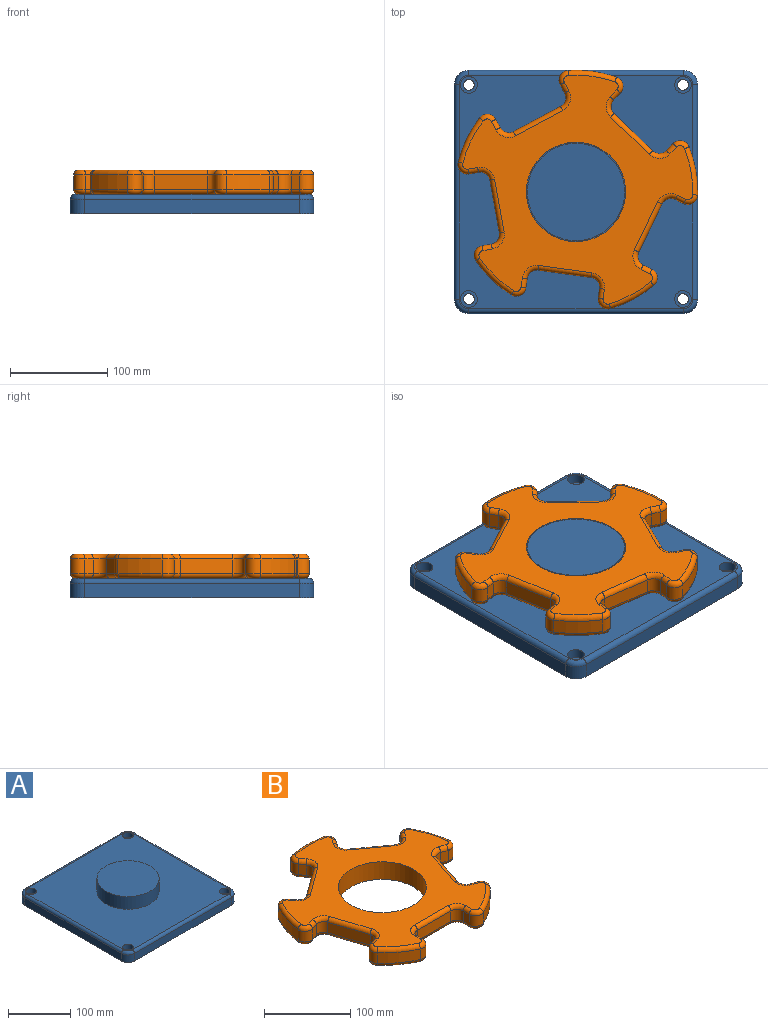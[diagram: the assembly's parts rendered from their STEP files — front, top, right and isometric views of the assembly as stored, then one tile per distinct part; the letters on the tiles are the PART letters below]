
ASSEMBLY  parts=2 mates=1
PART A: 32 faces, bbox 252.5x252.5x45 mm
  f0: plane 220x15mm, normal (1,0,0), area 3300mm2, adj f5,f8,f11,f27
  f1: plane 220x15mm, normal (0,1,0), area 3300mm2, adj f5,f8,f9,f31
  f2: plane 220x15mm, normal (-1,0,0), area 3300mm2, adj f5,f9,f10,f28
  f3: plane 220x15mm, normal (0,-1,0), area 3300mm2, adj f5,f10,f11,f24
  f4: plane 240x240mm, normal (0,0,1), area 48725.4mm2, adj f6,f14,f17,f20,f23,f24,f25,f26
  f5: plane 250x250mm, normal (0,0,-1), area 61926.7mm2, adj f0,f1,f2,f3,f8,f9,f10,f11
  f6: cylinder r=50mm len=100mm, axis (0,0,-1), area 7854mm2, adj f4,f7
  f7: plane 100x100mm, normal (0,0,1), area 7854mm2, adj f6
  f8: cylinder r=15mm len=15mm, axis (0,0,-1), area 353.4mm2, adj f0,f1,f5,f29
  f9: cylinder r=15mm len=15mm, axis (0,0,1), area 353.4mm2, adj f1,f2,f5,f30
  f10: cylinder r=15mm len=15mm, axis (0,0,-1), area 353.4mm2, adj f2,f3,f5,f26
  f11: cylinder r=15mm len=15mm, axis (0,0,1), area 353.4mm2, adj f0,f3,f5,f25
  f12: cylinder r=5.5mm len=11mm, axis (0,0,1), area 345.6mm2, adj f5,f13
  f13: plane 17.25x17.25mm, normal (0,0,1), area 138.7mm2, adj f12,f14
  f14: cylinder r=8.62mm len=17.25mm, axis (0,0,1), area 541.9mm2, adj f4,f13
  f15: cylinder r=5.5mm len=11mm, axis (0,0,1), area 345.6mm2, adj f5,f16
  f16: plane 17.25x17.25mm, normal (0,0,1), area 138.7mm2, adj f15,f17
  f17: cylinder r=8.62mm len=17.25mm, axis (0,0,1), area 541.9mm2, adj f4,f16
  f18: cylinder r=5.5mm len=11mm, axis (0,0,1), area 345.6mm2, adj f5,f19
  f19: plane 17.25x17.25mm, normal (0,0,1), area 138.7mm2, adj f18,f20
  f20: cylinder r=8.62mm len=17.25mm, axis (0,0,1), area 541.9mm2, adj f4,f19
  f21: cylinder r=5.5mm len=11mm, axis (0,0,1), area 345.6mm2, adj f5,f22
  f22: plane 17.25x17.25mm, normal (0,0,1), area 138.7mm2, adj f21,f23
  f23: cylinder r=8.62mm len=17.25mm, axis (0,0,1), area 541.9mm2, adj f4,f22
  f24: cylinder r=5mm len=220mm, axis (-1,0,0), area 1727.9mm2, adj f3,f4,f25,f26
  f25: torus R=10mm, axis (0,0,1), area 162.6mm2, adj f4,f11,f24,f27
  f26: torus R=10mm, axis (0,0,1), area 162.6mm2, adj f4,f10,f24,f28
  f27: cylinder r=5mm len=220mm, axis (0,-1,0), area 1727.9mm2, adj f0,f4,f25,f29
  f28: cylinder r=5mm len=220mm, axis (0,1,0), area 1727.9mm2, adj f2,f4,f26,f30
  f29: torus R=10mm, axis (0,0,1), area 162.6mm2, adj f4,f8,f27,f31
  f30: torus R=10mm, axis (0,0,1), area 162.6mm2, adj f4,f9,f28,f31
  f31: cylinder r=5mm len=220mm, axis (1,0,0), area 1727.9mm2, adj f1,f4,f29,f30
PART B: 123 faces, bbox 268.9x258.5x25 mm
  f0: plane 238.57x229.73mm, normal (0,0,1), area 21505.7mm2, adj f6,f43,f44,f45,f46,f47,f48,f49
  f1: plane 238.57x229.73mm, normal (0,0,-1), area 21505.7mm2, adj f6,f83,f84,f85,f86,f87,f88,f89
  f2: cylinder r=125mm len=40.68mm, axis (0,0,-1), area 759.5mm2, adj f13,f42,f51,f91
  f3: cylinder r=125mm len=47.82mm, axis (0,0,-1), area 759.5mm2, adj f35,f41,f67,f107
  f4: cylinder r=125mm len=50.29mm, axis (0,0,-1), area 759.5mm2, adj f28,f34,f82,f122
  f5: cylinder r=125mm len=47.82mm, axis (0,0,-1), area 759.5mm2, adj f21,f27,f66,f106
  f6: cylinder r=51mm len=102mm, axis (0,0,-1), area 8011.1mm2, adj f0,f1
  f7: cylinder r=125mm len=40.68mm, axis (0,0,-1), area 759.5mm2, adj f14,f20,f50,f90
  f8: plane 15x9.73mm, normal (-1,0,0), area 146mm2, adj f11,f14,f46,f86
  f9: plane 55x15mm, normal (0,-1,0), area 825mm2, adj f11,f12,f43,f83
  f10: plane 15x9.73mm, normal (1,0,0), area 146mm2, adj f12,f13,f47,f87
  f11: cylinder r=10mm len=15mm, axis (0,0,-1), area 235.6mm2, adj f8,f9,f44,f84
  f12: cylinder r=10mm len=15mm, axis (0,0,-1), area 235.6mm2, adj f9,f10,f45,f85
  f13: cylinder r=10mm len=15mm, axis (0,0,-1), area 299.5mm2, adj f2,f10,f49,f89
  f14: cylinder r=10mm len=15mm, axis (0,0,-1), area 299.5mm2, adj f7,f8,f48,f88
  f15: plane 15x9.26mm, normal (-0.31,-0.95,0), area 146mm2, adj f18,f21,f62,f102
  f16: plane 52.31x17mm, normal (0.95,-0.31,0), area 825mm2, adj f18,f19,f58,f98
  f17: plane 15x9.26mm, normal (0.31,0.95,0), area 146mm2, adj f19,f20,f54,f94
  f18: cylinder r=10mm len=15mm, axis (0,0,-1), area 235.6mm2, adj f15,f16,f60,f100
  f19: cylinder r=10mm len=15mm, axis (0,0,-1), area 235.6mm2, adj f16,f17,f56,f96
  f20: cylinder r=10mm len=16.25mm, axis (0,0,-1), area 299.5mm2, adj f7,f17,f52,f92
  f21: cylinder r=10mm len=15mm, axis (0,0,-1), area 299.5mm2, adj f5,f15,f64,f104
  f22: plane 15x7.87mm, normal (0.81,-0.59,0), area 146mm2, adj f25,f28,f78,f118
  f23: plane 44.5x32.33mm, normal (0.59,0.81,0), area 825mm2, adj f25,f26,f74,f114
  f24: plane 15x7.87mm, normal (-0.81,0.59,0), area 146mm2, adj f26,f27,f70,f110
  f25: cylinder r=10mm len=15mm, axis (0,0,-1), area 235.6mm2, adj f22,f23,f76,f116
  f26: cylinder r=10mm len=15mm, axis (0,0,-1), area 235.6mm2, adj f23,f24,f72,f112
  f27: cylinder r=10mm len=16.78mm, axis (0,0,-1), area 299.5mm2, adj f5,f24,f68,f108
  f28: cylinder r=10mm len=15.67mm, axis (0,0,-1), area 299.5mm2, adj f4,f22,f80,f120
  f29: plane 15x7.87mm, normal (0.81,0.59,0), area 146mm2, adj f32,f35,f71,f111
  f30: plane 44.5x32.33mm, normal (-0.59,0.81,0), area 825mm2, adj f32,f33,f75,f115
  f31: plane 15x7.87mm, normal (-0.81,-0.59,0), area 146mm2, adj f33,f34,f79,f119
  f32: cylinder r=10mm len=15mm, axis (0,0,-1), area 235.6mm2, adj f29,f30,f73,f113
  f33: cylinder r=10mm len=15mm, axis (0,0,-1), area 235.6mm2, adj f30,f31,f77,f117
  f34: cylinder r=10mm len=15.67mm, axis (0,0,-1), area 299.5mm2, adj f4,f31,f81,f121
  f35: cylinder r=10mm len=16.78mm, axis (0,0,-1), area 299.5mm2, adj f3,f29,f69,f109
  f36: plane 15x9.26mm, normal (-0.31,0.95,0), area 146mm2, adj f39,f42,f55,f95
  f37: plane 52.31x17mm, normal (-0.95,-0.31,0), area 825mm2, adj f39,f40,f59,f99
  f38: plane 15x9.26mm, normal (0.31,-0.95,0), area 146mm2, adj f40,f41,f63,f103
  f39: cylinder r=10mm len=15mm, axis (0,0,-1), area 235.6mm2, adj f36,f37,f57,f97
  f40: cylinder r=10mm len=15mm, axis (0,0,-1), area 235.6mm2, adj f37,f38,f61,f101
  f41: cylinder r=10mm len=15mm, axis (0,0,-1), area 299.5mm2, adj f3,f38,f65,f105
  f42: cylinder r=10mm len=16.25mm, axis (0,0,-1), area 299.5mm2, adj f2,f36,f53,f93
  f43: cylinder r=5mm len=55mm, axis (1,0,0), area 432mm2, adj f0,f9,f44,f45
  f44: torus R=15mm, axis (0,0,1), area 145.8mm2, adj f0,f11,f43,f46
  f45: torus R=15mm, axis (0,0,1), area 145.8mm2, adj f0,f12,f43,f47
  f46: cylinder r=5mm len=9.73mm, axis (0,-1,0), area 76.4mm2, adj f0,f8,f44,f48
  f47: cylinder r=5mm len=9.73mm, axis (0,1,0), area 76.4mm2, adj f0,f10,f45,f49
  f48: torus R=5mm, axis (0,0,1), area 128.3mm2, adj f0,f14,f46,f50
  f49: torus R=5mm, axis (0,0,1), area 128.3mm2, adj f0,f13,f47,f51
  f50: torus R=120mm, axis (0,0,1), area 391.9mm2, adj f0,f7,f48,f52
  f51: torus R=120mm, axis (0,0,1), area 391.9mm2, adj f0,f2,f49,f53
  f52: torus R=5mm, axis (0,0,1), area 128.3mm2, adj f0,f20,f50,f54
  f53: torus R=5mm, axis (0,0,1), area 128.3mm2, adj f0,f42,f51,f55
  f54: cylinder r=5mm len=10.8mm, axis (-0.95,0.31,0), area 76.4mm2, adj f0,f17,f52,f56
  f55: cylinder r=5mm len=10.8mm, axis (-0.95,-0.31,0), area 76.4mm2, adj f0,f36,f53,f57
  f56: torus R=15mm, axis (0,0,1), area 145.8mm2, adj f0,f19,f54,f58
  f57: torus R=15mm, axis (0,0,1), area 145.8mm2, adj f0,f39,f55,f59
  f58: cylinder r=5mm len=53.85mm, axis (0.31,0.95,0), area 432mm2, adj f0,f16,f56,f60
  f59: cylinder r=5mm len=53.85mm, axis (0.31,-0.95,0), area 432mm2, adj f0,f37,f57,f61
  f60: torus R=15mm, axis (0,0,1), area 145.8mm2, adj f0,f18,f58,f62
  f61: torus R=15mm, axis (0,0,1), area 145.8mm2, adj f0,f40,f59,f63
  f62: cylinder r=5mm len=10.8mm, axis (0.95,-0.31,0), area 76.4mm2, adj f0,f15,f60,f64
  f63: cylinder r=5mm len=10.8mm, axis (0.95,0.31,0), area 76.4mm2, adj f0,f38,f61,f65
  f64: torus R=5mm, axis (0,0,1), area 128.3mm2, adj f0,f21,f62,f66
  f65: torus R=5mm, axis (0,0,1), area 128.3mm2, adj f0,f41,f63,f67
  f66: torus R=120mm, axis (0,0,1), area 391.9mm2, adj f0,f5,f64,f68
  f67: torus R=120mm, axis (0,0,1), area 391.9mm2, adj f0,f3,f65,f69
  f68: torus R=5mm, axis (0,0,1), area 128.3mm2, adj f0,f27,f66,f70
  f69: torus R=5mm, axis (0,0,1), area 128.3mm2, adj f0,f35,f67,f71
  f70: cylinder r=5mm len=10.81mm, axis (-0.59,-0.81,0), area 76.4mm2, adj f0,f24,f68,f72
  f71: cylinder r=5mm len=10.81mm, axis (-0.59,0.81,0), area 76.4mm2, adj f0,f29,f69,f73
  f72: torus R=15mm, axis (0,0,1), area 145.8mm2, adj f0,f26,f70,f74
  f73: torus R=15mm, axis (0,0,1), area 145.8mm2, adj f0,f32,f71,f75
  f74: cylinder r=5mm len=47.44mm, axis (-0.81,0.59,0), area 432mm2, adj f0,f23,f72,f76
  f75: cylinder r=5mm len=47.44mm, axis (-0.81,-0.59,0), area 432mm2, adj f0,f30,f73,f77
  f76: torus R=15mm, axis (0,0,1), area 145.8mm2, adj f0,f25,f74,f78
  f77: torus R=15mm, axis (0,0,1), area 145.8mm2, adj f0,f33,f75,f79
  f78: cylinder r=5mm len=10.81mm, axis (0.59,0.81,0), area 76.4mm2, adj f0,f22,f76,f80
  f79: cylinder r=5mm len=10.81mm, axis (0.59,-0.81,0), area 76.4mm2, adj f0,f31,f77,f81
  f80: torus R=5mm, axis (0,0,1), area 128.3mm2, adj f0,f28,f78,f82
  f81: torus R=5mm, axis (0,0,1), area 128.3mm2, adj f0,f34,f79,f82
  f82: torus R=120mm, axis (0,0,1), area 391.9mm2, adj f0,f4,f80,f81
  f83: cylinder r=5mm len=55mm, axis (-1,0,0), area 432mm2, adj f1,f9,f84,f85
  f84: torus R=15mm, axis (0,0,1), area 145.8mm2, adj f1,f11,f83,f86
  f85: torus R=15mm, axis (0,0,1), area 145.8mm2, adj f1,f12,f83,f87
  f86: cylinder r=5mm len=9.73mm, axis (0,1,0), area 76.4mm2, adj f1,f8,f84,f88
  f87: cylinder r=5mm len=9.73mm, axis (0,-1,0), area 76.4mm2, adj f1,f10,f85,f89
  f88: torus R=5mm, axis (0,0,1), area 128.3mm2, adj f1,f14,f86,f90
  f89: torus R=5mm, axis (0,0,1), area 128.3mm2, adj f1,f13,f87,f91
  f90: torus R=120mm, axis (0,0,1), area 391.9mm2, adj f1,f7,f88,f92
  f91: torus R=120mm, axis (0,0,1), area 391.9mm2, adj f1,f2,f89,f93
  f92: torus R=5mm, axis (0,0,1), area 128.3mm2, adj f1,f20,f90,f94
  f93: torus R=5mm, axis (0,0,1), area 128.3mm2, adj f1,f42,f91,f95
  f94: cylinder r=5mm len=10.8mm, axis (0.95,-0.31,0), area 76.4mm2, adj f1,f17,f92,f96
  f95: cylinder r=5mm len=10.8mm, axis (0.95,0.31,0), area 76.4mm2, adj f1,f36,f93,f97
  f96: torus R=15mm, axis (0,0,1), area 145.8mm2, adj f1,f19,f94,f98
  f97: torus R=15mm, axis (0,0,1), area 145.8mm2, adj f1,f39,f95,f99
  f98: cylinder r=5mm len=53.85mm, axis (-0.31,-0.95,0), area 432mm2, adj f1,f16,f96,f100
  f99: cylinder r=5mm len=53.85mm, axis (-0.31,0.95,0), area 432mm2, adj f1,f37,f97,f101
  f100: torus R=15mm, axis (0,0,1), area 145.8mm2, adj f1,f18,f98,f102
  f101: torus R=15mm, axis (0,0,1), area 145.8mm2, adj f1,f40,f99,f103
  f102: cylinder r=5mm len=10.8mm, axis (-0.95,0.31,0), area 76.4mm2, adj f1,f15,f100,f104
  f103: cylinder r=5mm len=10.8mm, axis (-0.95,-0.31,0), area 76.4mm2, adj f1,f38,f101,f105
  f104: torus R=5mm, axis (0,0,1), area 128.3mm2, adj f1,f21,f102,f106
  f105: torus R=5mm, axis (0,0,1), area 128.3mm2, adj f1,f41,f103,f107
  f106: torus R=120mm, axis (0,0,1), area 391.9mm2, adj f1,f5,f104,f108
  f107: torus R=120mm, axis (0,0,1), area 391.9mm2, adj f1,f3,f105,f109
  f108: torus R=5mm, axis (0,0,1), area 128.3mm2, adj f1,f27,f106,f110
  f109: torus R=5mm, axis (0,0,1), area 128.3mm2, adj f1,f35,f107,f111
  f110: cylinder r=5mm len=10.81mm, axis (0.59,0.81,0), area 76.4mm2, adj f1,f24,f108,f112
  f111: cylinder r=5mm len=10.81mm, axis (0.59,-0.81,0), area 76.4mm2, adj f1,f29,f109,f113
  f112: torus R=15mm, axis (0,0,1), area 145.8mm2, adj f1,f26,f110,f114
  f113: torus R=15mm, axis (0,0,1), area 145.8mm2, adj f1,f32,f111,f115
  f114: cylinder r=5mm len=47.44mm, axis (0.81,-0.59,0), area 432mm2, adj f1,f23,f112,f116
  f115: cylinder r=5mm len=47.44mm, axis (0.81,0.59,0), area 432mm2, adj f1,f30,f113,f117
  f116: torus R=15mm, axis (0,0,1), area 145.8mm2, adj f1,f25,f114,f118
  f117: torus R=15mm, axis (0,0,1), area 145.8mm2, adj f1,f33,f115,f119
  f118: cylinder r=5mm len=10.81mm, axis (-0.59,-0.81,0), area 76.4mm2, adj f1,f22,f116,f120
  f119: cylinder r=5mm len=10.81mm, axis (-0.59,0.81,0), area 76.4mm2, adj f1,f31,f117,f121
  f120: torus R=5mm, axis (0,0,1), area 128.3mm2, adj f1,f28,f118,f122
  f121: torus R=5mm, axis (0,0,1), area 128.3mm2, adj f1,f34,f119,f122
  f122: torus R=120mm, axis (0,0,1), area 391.9mm2, adj f1,f4,f120,f121
PLACE A at identity fixed
PLACE B rot(axis=(0,0,1),64.1deg) t=(0,0,0)mm
MATE revolute B.f2 <-> A.f6  axis (0,0,-1) through (0,0,20)mm
